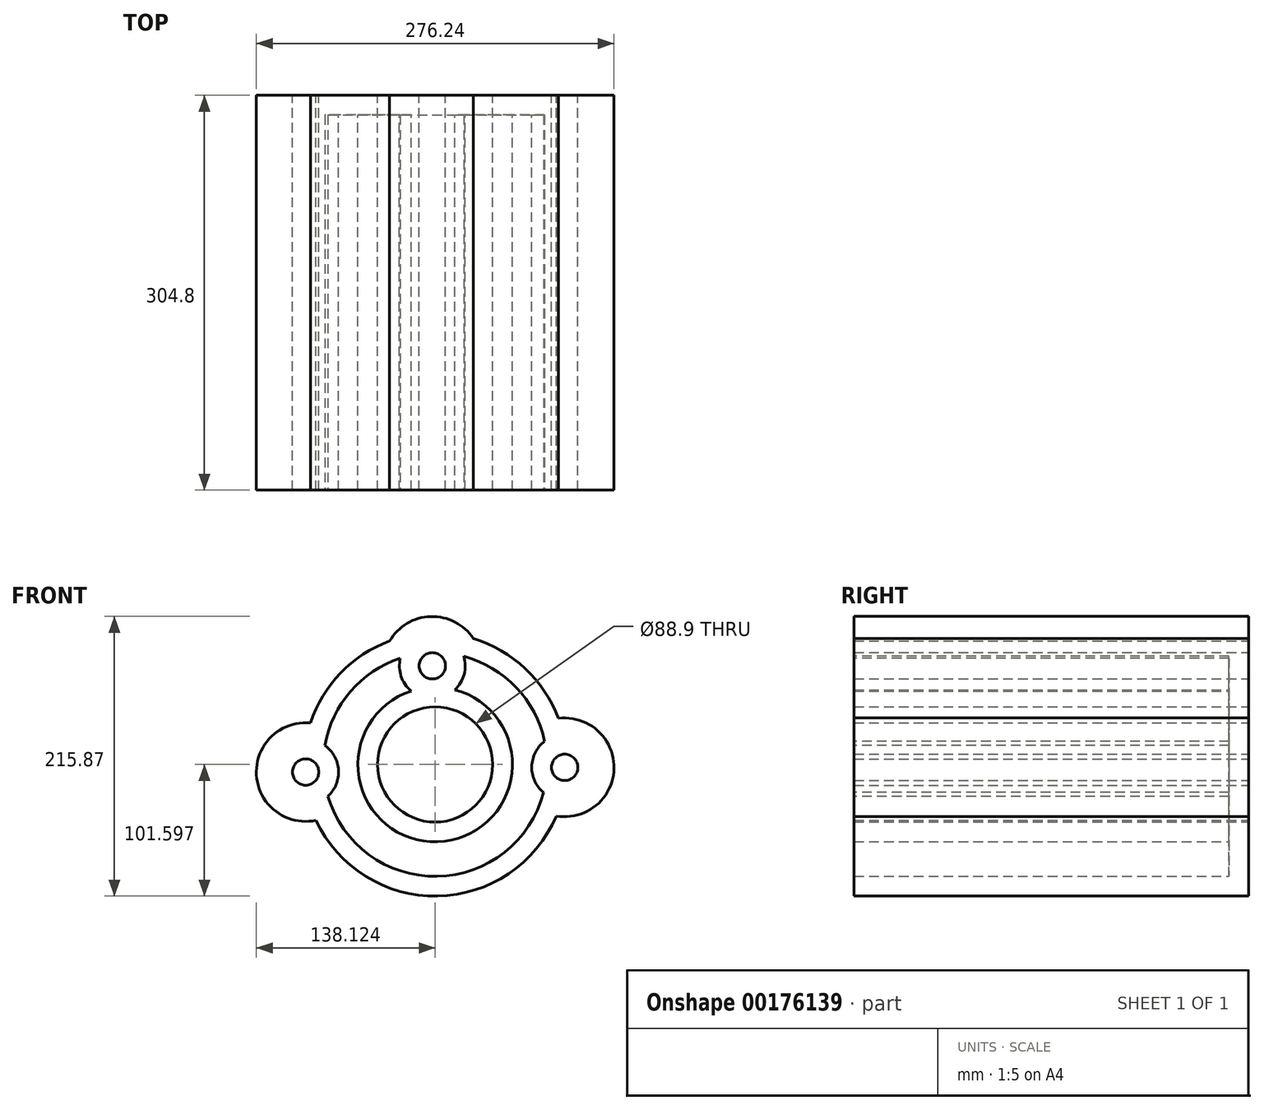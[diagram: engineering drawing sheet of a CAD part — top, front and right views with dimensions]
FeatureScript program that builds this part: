
annotation { "Feature Type Name" : "Feature", "Feature Type Description" : "" }
export const myFeature = defineFeature(function(context is Context, id is Id, definition is map)
    precondition{}
    {
        {
            var Q0;
            Q0=qCreatedBy(makeId("Front.planeOp"),FACE);
            var sketch = newSketch(context, id + "F0", { "sketchPlane" : qUnion([Q0])});
            skCircle(sketch, "E0", {"center": v(101.6, -33.71) * mm, "radius": 10.16 * mm});
            skCircle(sketch, "E1", {"center": v(3.79, -115.72) * mm, "radius": 10.16 * mm});
            skCircle(sketch, "E2", {"center": v(203.83, -112.08) * mm, "radius": 10.16 * mm});
            skCircle(sketch, "E3", {"center": v(103.81, -109.88) * mm, "radius": 44.45 * mm});
            skArc(sketch, "E4", {"start": v(7.41, -77.8) * mm, "mid": v(-34.25, -117.94) * mm, "end": v(11.8, -152.97) * mm});
            skArc(sketch, "E5", {"start": v(197.32, -149.62) * mm, "mid": v(241.92, -112.92) * mm, "end": v(198.98, -74.29) * mm});
            skArc(sketch, "E6", {"start": v(133.36, -12.67) * mm, "mid": v(100.5, 4.37) * mm, "end": v(68.67, -14.56) * mm});
            skArc(sketch, "E7", {"start": v(68.67, -14.56) * mm, "mid": v(30.83, -39.2) * mm, "end": v(7.41, -77.8) * mm});
            skPoint(sketch, "E8.orphan", {"position": v(203.2, 0) * mm});
            skArc(sketch, "E9.trimOffspring", {"start": v(198.98, -74.29) * mm, "mid": v(173.36, -35.82) * mm, "end": v(133.36, -12.67) * mm});
            skArc(sketch, "E10.trimOffspring", {"start": v(11.8, -152.97) * mm, "mid": v(105.65, -211.47) * mm, "end": v(197.32, -149.62) * mm});
            skSolve(sketch);
        }
        {
            var Q0;
            Q0=makeQuery(id+"F0.imprint","IMPRINT",FACE,{"disambiguationData":[TD([[makeQuery(id+"F0.imprint","IMPRINT",EDGE,{"derivedFrom":sQuery(id+"F0.wireOp",EDGE,"E0")}),-1.0]])]});
            extrude(context, id + "F1", {"entities" : qUnion([Q0]), "depth" : 304.8 * mm});
        }
        {
            var Q0;
            Q0=makeQuery(id+"F1.opExtrude","CAP_FACE",FACE,{"disambiguationData":[OSD([sQuery(id+"F0.wireOp",EDGE,"E0"),sQuery(id+"F0.wireOp",EDGE,"E1"),sQuery(id+"F0.wireOp",EDGE,"E2"),sQuery(id+"F0.wireOp",EDGE,"E3"),sQuery(id+"F0.wireOp",EDGE,"E4"),sQuery(id+"F0.wireOp",EDGE,"E5"),sQuery(id+"F0.wireOp",EDGE,"E6"),sQuery(id+"F0.wireOp",EDGE,"E7"),sQuery(id+"F0.wireOp",EDGE,"E9.trimOffspring"),sQuery(id+"F0.wireOp",EDGE,"E10.trimOffspring")])],"isStart":false});
            shell(context, id + "F2", {"entities" : qUnion([Q0]), "thickness" : 15.24 * mm});
        }
    });
